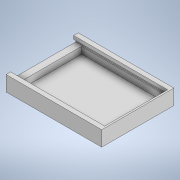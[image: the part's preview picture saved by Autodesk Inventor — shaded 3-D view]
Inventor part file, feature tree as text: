
AUTODESK INVENTOR PART (.ipt)
format: ipt  version: 2021 (Build 250183000, 183)  size: 319,488 bytes
history: native  units: mm
features: extrude x15, sketch x15, other x1
ambient origin geometry x8: Origin, YZ Plane, XZ Plane, XY Plane, X Axis, Y Axis, Z Axis, Center Point
bodies: Body1 (feature_tree)
feature tree (31):
  other  "Sólido1"
  extrude  "Extrusión1"  Depth=41.0mm
  extrude  "Extrusión2"  Depth=8.0mm
  extrude  "Extrusión3"  Depth=2.0mm
  extrude  "Extrusión4"  Depth=6.0mm TaperAngle=0.0deg
  extrude  "Extrusión5"  Depth=6.0mm TaperAngle=0.0deg
  extrude  "Extrusión6"  Depth=1.0mm
  extrude  "Extrusión7"  Depth=1.0mm TaperAngle=0.0deg
  extrude  "Extrusión8"  Depth=1.0mm
  extrude  "Extrusión9"  Depth=1.0mm TaperAngle=0.0deg
  extrude  "Extrusión10"  Depth=2.0mm
  extrude  "Extrusión11"  Depth=1.0mm TaperAngle=0.0deg
  extrude  "Extrusión12"  Depth=1.0mm
  extrude  "Extrusión13"  Depth=1.0mm TaperAngle=0.0deg
  extrude  "Extrusión14"  Depth=4.0mm
  extrude  "Extrusión15"  Depth=1.0mm
  sketch  "Boceto1"  dims[d0=57.0mm d1=41.0mm]
  sketch  "Boceto2"  dims[d2=8.0mm d3=0.0mm d4=3.0mm]
  sketch  "Boceto3"  dims[d5=2.0mm d6=35.0mm]
  sketch  "Boceto4"  dims[d7=51.0mm d8=6.0mm d9=0.0mm]
  sketch  "Boceto5"  dims[d10=35.0mm d11=6.0mm d12=0.0mm]
  sketch  "Boceto6"  dims[d13=1.0mm d14=1.0mm]
  sketch  "Boceto7"  dims[d15=1.0mm d16=55.0mm d17=0.0mm]
  sketch  "Boceto8"  dims[d18=1.0mm d19=1.0mm]
  sketch  "Boceto9"  dims[d20=1.0mm d21=55.0mm d22=0.0mm]
  sketch  "Boceto10"  dims[d23=2.0mm d24=2.0mm]
  sketch  "Boceto11"  dims[d25=1.0mm d26=55.0mm d27=0.0mm]
  sketch  "Boceto12"  dims[d28=2.0mm d29=1.0mm]
  sketch  "Boceto13"  dims[d30=55.0mm d31=0.0mm d32=1.0mm d33=0.0mm]
  sketch  "Boceto14"  dims[d34=4.0mm d35=0.0mm d36=42.0mm]
  sketch  "Boceto15"  dims[d37=8.0mm d38=1.0mm d39=2.0mm d40=2.0mm d41=2.0mm d42=57.0mm d43=0.0mm d44=1.0mm d45=2.0mm d46=41.0mm d47=56.0mm d48=0.0mm d49=1.0mm d50=0.0mm d51=52.0mm d52=4.0mm d53=0.0mm d54=0.75mm d55=2.0mm d56=40.0mm d57=1.25mm d58=4.0mm d59=0.0mm d60=53.0mm d61=0.0mm]
